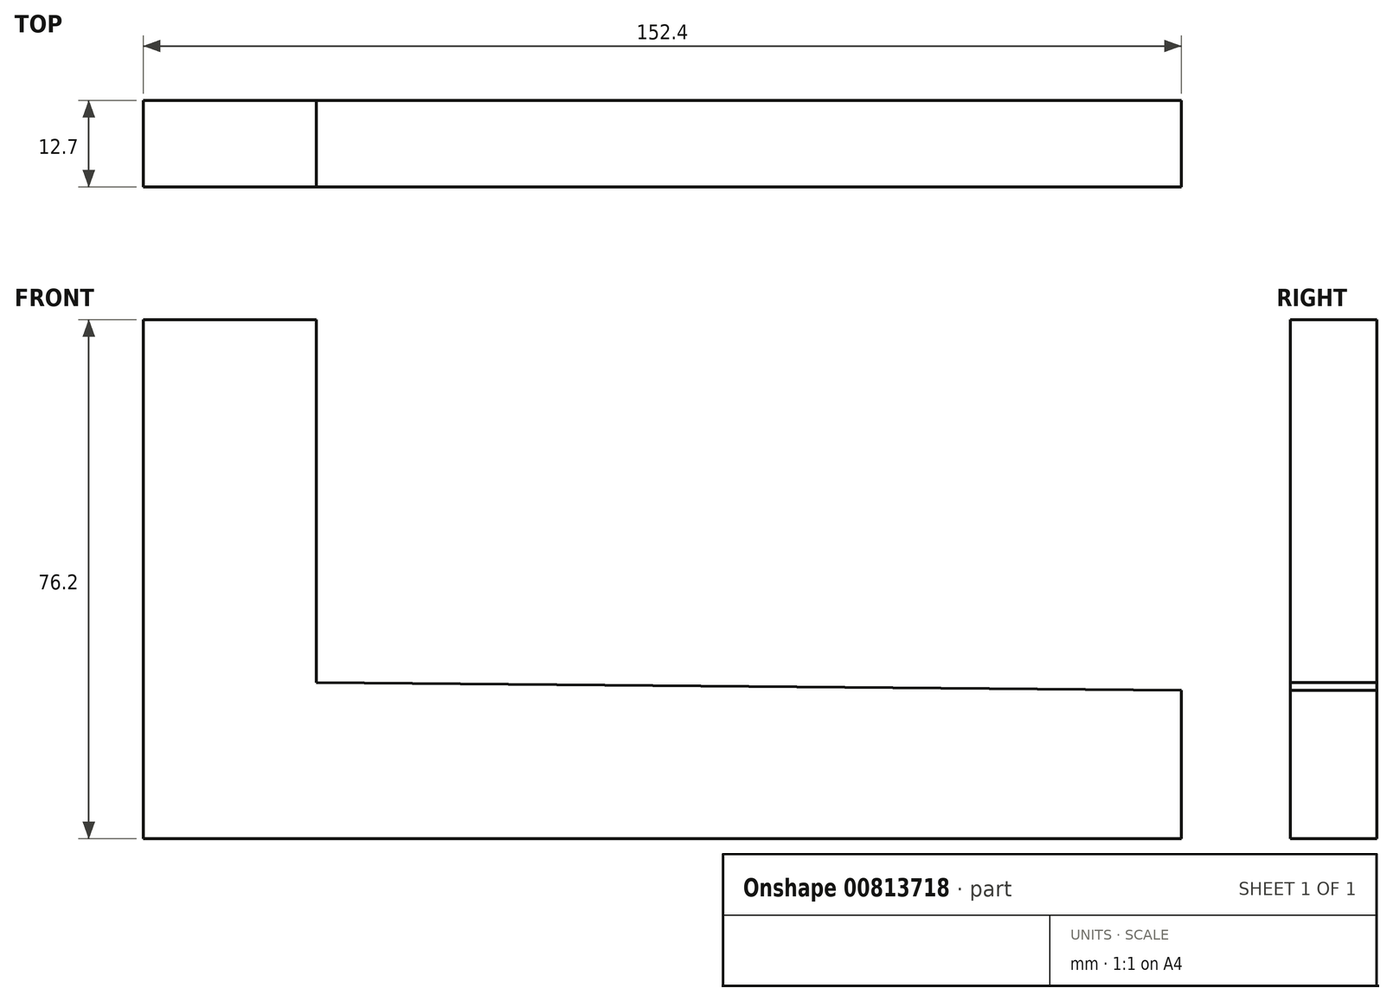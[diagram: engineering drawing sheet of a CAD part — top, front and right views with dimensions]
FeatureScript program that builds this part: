
annotation { "Feature Type Name" : "Feature", "Feature Type Description" : "" }
export const myFeature = defineFeature(function(context is Context, id is Id, definition is map)
    precondition{}
    {
        {
            var Q0;
            Q0=qCreatedBy(makeId("Front.planeOp"),FACE);
            var sketch = newSketch(context, id + "F0", { "sketchPlane" : qUnion([Q0])});
            skLineSegment(sketch, "E0", {"start": v(-106.64, 54.4) * mm, "end": v(-106.64, -21.8) * mm});
            skLineSegment(sketch, "E1", {"start": v(-106.64, -21.8) * mm, "end": v(45.76, -21.8) * mm});
            skLineSegment(sketch, "E2", {"start": v(45.76, -21.8) * mm, "end": v(45.76, 0) * mm});
            skLineSegment(sketch, "E3", {"start": v(45.76, 0) * mm, "end": v(-81.24, 1.1) * mm});
            skLineSegment(sketch, "E4", {"start": v(-81.24, 1.1) * mm, "end": v(-81.24, 54.4) * mm});
            skLineSegment(sketch, "E5", {"start": v(-81.24, 54.4) * mm, "end": v(-106.64, 54.4) * mm});
            skSolve(sketch);
        }
        {
            var Q0;
            Q0=makeQuery(id+"F0.imprint","IMPRINT",FACE,{"disambiguationData":[TD([[makeQuery(id+"F0.imprint","IMPRINT",EDGE,{"derivedFrom":sQuery(id+"F0.wireOp",EDGE,"E0")}),1.0]])]});
            extrude(context, id + "F1", {"entities" : qUnion([Q0]), "depth" : 12.7 * mm, "offsetDistance" : 25.4 * mm});
        }
    });
